# Revit family: 11Construction_Fences-&-Traffic-Security_AutoGate_Catawba-Pivot-Gates
name_source: partatom
category: Specialty Equipment
units: mm (PartAtom-declared; Revit-internal decimal feet)

## family parameters
Always vertical = Yes
Cut with Voids When Loaded = No
Enable Cutting in Views = Yes
Maintain Annotation Orientation = No
OmniClass Number = 23.25.40.21.21
OmniClass Title = Gates
Part Type = Normal
Room Calculation Point = No
Round Connector Dimension = Use Diameter
Shared = No
Work Plane-Based = Yes

## types (4) — shared parameters
Assembly Code = G2040100
Date Updated = 2025/09/08
Description = Catawba Vertcal Pivot Gate
Installation instructions = https://www.itwredhead.com
Keynote = 321000
Manufacturer = AutoGate
Product Documentation Link = https://www.itwredhead.com
Product Page URL = https://www.autogate.com
Product data url = https://bimobject.com
URL = https://www.autogate.com
Version = 1
z_Picket Thickness = 0.75 "
zero-valued in all types: Default Elevation

## per-type parameters (varying)
| type | Model | z_Concave Curve | z_Concave Void | z_Concave Void with Finials | z_Convex Curve | z_Convex Void | z_Convex Void with Finials | z_Finials DI | z_Type Index |
| Catawba Concave VPG | Catawba - Concave VPG | Yes | Yes | No | No | No | No | No | 1 |
| Catawba Convex VPG | Catawba - Convex VPG | No | No | No | Yes | Yes | No | No | 3 |
| Catawba Concave VPG with Finials | Catawba - Concave VPG with Finials | Yes | No | Yes | No | No | No | Yes | 2 |
| Catawba Convex VPG with Finials | Catawba - Convex VPG with Finials | No | No | No | Yes | No | Yes | Yes | 4 |

## geometry (parser evidence)
native form markers: Sweep x7
no freeform markers — native parametric forms only
